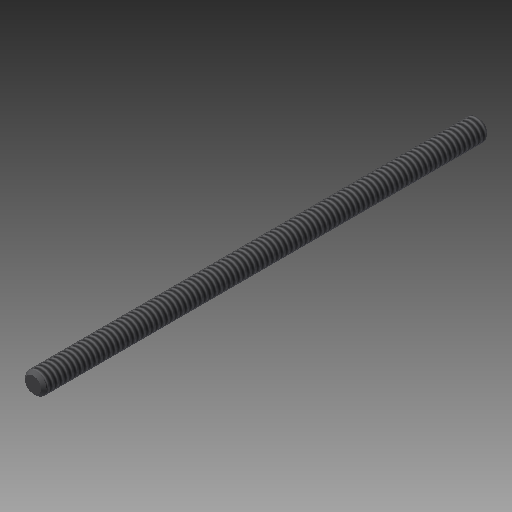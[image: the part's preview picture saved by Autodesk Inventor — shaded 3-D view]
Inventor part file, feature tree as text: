
AUTODESK INVENTOR PART (.ipt)
format: ipt  version: 2017 (Build 210142000, 142)  size: 117,248 bytes
history: native  units: in
note: dims shown in document units (in); Inventor stores cm internally (conversion verified against a paired STEP export)
features: other x7, revolve x1, thread x1, sketch x1
ambient origin geometry x8: Origin, YZ Plane, XZ Plane, XY Plane, X Axis, Y Axis, Z Axis, Center Point
bodies: Solid1 (feature_tree)
feature tree (10):
  revolve  "Revolution1"  [1 undecoded]
  thread  "Thread1"  [1 undecoded]
  other  "screw_XY"
  other  "screw_YZ"
  other  "screw_ZX"
  other  "screw_X"
  other  "screw_Y"
  other  "screw_Z"
  other  "screw_Center"
  sketch  "Sketch_1"  dims[d0=360.0deg d1=2.2872in d2=0.0in]
note: 2 required parameter values undecoded (feature->parameter linkage not recoverable at this tier; creation-order binding heuristic only, values carry confidence <= 0.55)